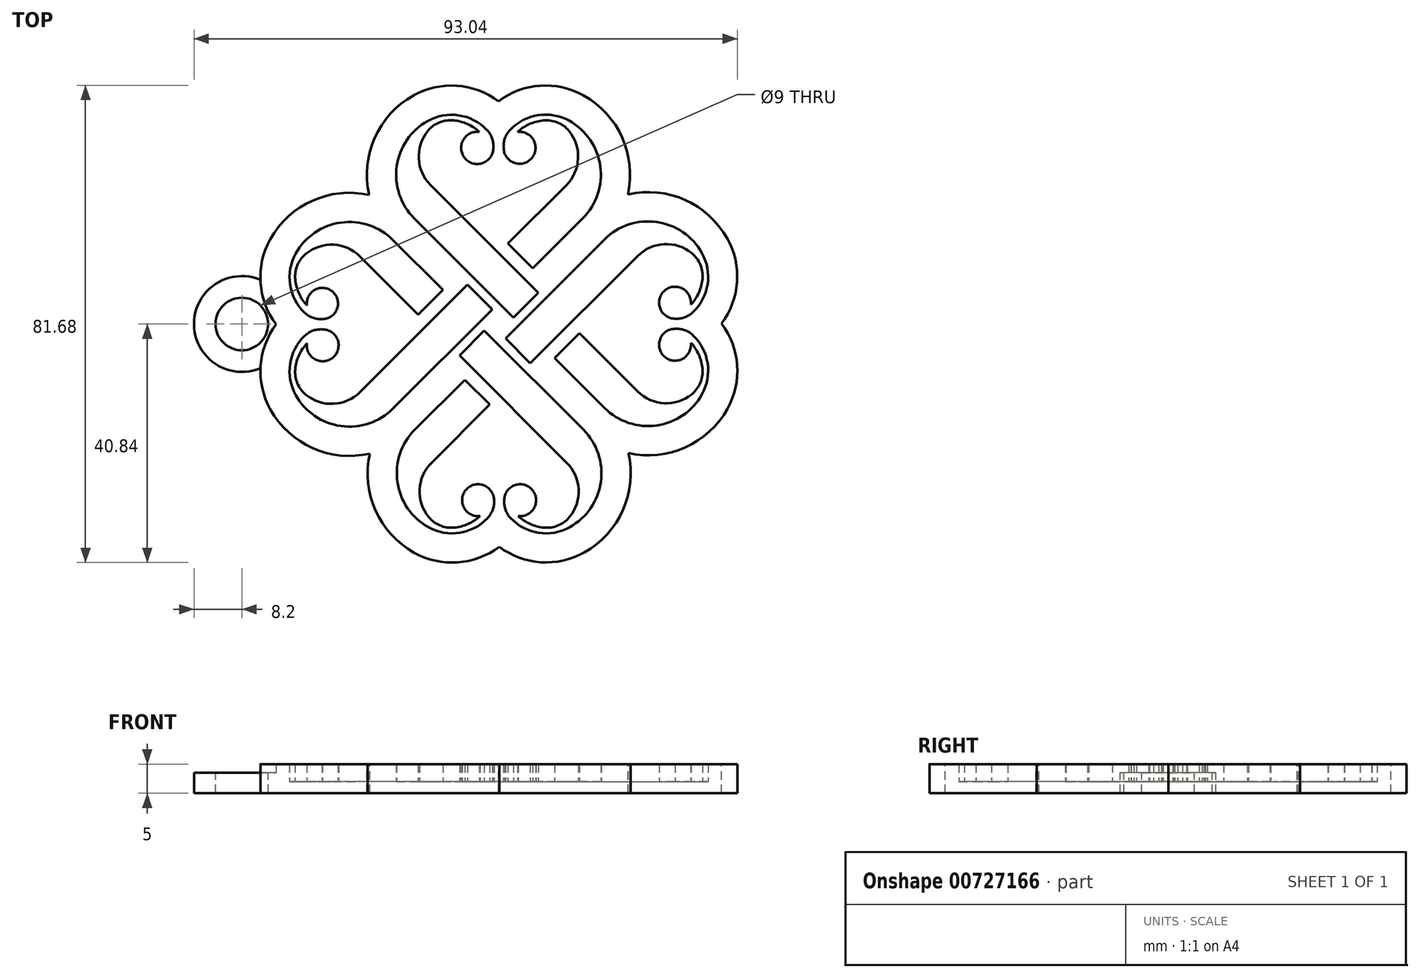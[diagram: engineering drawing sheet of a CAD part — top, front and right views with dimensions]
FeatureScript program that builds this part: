
annotation { "Feature Type Name" : "Feature", "Feature Type Description" : "" }
export const myFeature = defineFeature(function(context is Context, id is Id, definition is map)
    precondition{}
    {
        {
            var Q0;
            Q0=qCreatedBy(makeId("Top.planeOp"),FACE);
            var sketch = newSketch(context, id + "F0", { "sketchPlane" : qUnion([Q0])});
            skLineSegment(sketch, "E0", {"start": v(2.5, 1.1) * mm, "end": v(6.73, 5.35) * mm});
            skLineSegment(sketch, "E1", {"start": v(2.5, 1.1) * mm, "end": v(-14.5, 18.1) * mm});
            skLineSegment(sketch, "E2", {"start": v(6.73, 5.35) * mm, "end": v(-11.69, 23.78) * mm});
            skArc(sketch, "E3", {"start": v(-11.69, 23.78) * mm, "mid": v(-13.7, 28.32) * mm, "end": v(-12.15, 33.05) * mm});
            skArc(sketch, "E4", {"start": v(-12.15, 33.05) * mm, "mid": v(-10.18, 34.5) * mm, "end": v(-7.75, 34.87) * mm});
            skArc(sketch, "E5", {"start": v(-7.75, 34.87) * mm, "mid": v(-5.39, 34.24) * mm, "end": v(-3.34, 32.88) * mm});
            skArc(sketch, "E6", {"start": v(-14.5, 18.1) * mm, "mid": v(-17.48, 27) * mm, "end": v(-12.18, 34.76) * mm});
            skArc(sketch, "E7", {"start": v(-12.18, 34.76) * mm, "mid": v(-6.85, 35.73) * mm, "end": v(-2.04, 33.22) * mm});
            skArc(sketch, "E8", {"start": v(-3.34, 32.88) * mm, "mid": v(-5.75, 28.32) * mm, "end": v(-0.94, 30.19) * mm});
            skArc(sketch, "E9", {"start": v(-2.04, 33.22) * mm, "mid": v(-1.17, 31.82) * mm, "end": v(-0.94, 30.19) * mm});
            skLineSegment(sketch, "E10", {"start": v(1.14, -2.5) * mm, "end": v(5.39, -6.73) * mm});
            skLineSegment(sketch, "E11", {"start": v(1.14, -2.5) * mm, "end": v(18.11, 14.48) * mm});
            skLineSegment(sketch, "E12", {"start": v(5.39, -6.73) * mm, "end": v(23.77, 11.65) * mm});
            skArc(sketch, "E13", {"start": v(23.77, 11.65) * mm, "mid": v(28.31, 13.67) * mm, "end": v(33.03, 12.12) * mm});
            skArc(sketch, "E14", {"start": v(33.03, 12.12) * mm, "mid": v(34.5, 10.15) * mm, "end": v(34.86, 7.72) * mm});
            skArc(sketch, "E15", {"start": v(34.86, 7.72) * mm, "mid": v(34.23, 5.35) * mm, "end": v(32.88, 3.3) * mm});
            skArc(sketch, "E16", {"start": v(18.11, 14.48) * mm, "mid": v(27.02, 17.47) * mm, "end": v(34.78, 12.16) * mm});
            skArc(sketch, "E17", {"start": v(34.78, 12.16) * mm, "mid": v(35.74, 6.83) * mm, "end": v(33.24, 2.02) * mm});
            skArc(sketch, "E18", {"start": v(32.88, 3.3) * mm, "mid": v(28.35, 5.69) * mm, "end": v(30.2, 0.92) * mm});
            skArc(sketch, "E19", {"start": v(33.24, 2.02) * mm, "mid": v(31.84, 1.15) * mm, "end": v(30.2, 0.92) * mm});
            skLineSegment(sketch, "E20", {"start": v(-2.5, -1.14) * mm, "end": v(-6.73, -5.39) * mm});
            skLineSegment(sketch, "E21", {"start": v(-2.5, -1.14) * mm, "end": v(14.48, -18.11) * mm});
            skLineSegment(sketch, "E22", {"start": v(-6.73, -5.39) * mm, "end": v(11.65, -23.77) * mm});
            skArc(sketch, "E23", {"start": v(11.65, -23.77) * mm, "mid": v(13.67, -28.31) * mm, "end": v(12.12, -33.03) * mm});
            skArc(sketch, "E24", {"start": v(12.12, -33.03) * mm, "mid": v(10.15, -34.5) * mm, "end": v(7.72, -34.86) * mm});
            skArc(sketch, "E25", {"start": v(7.72, -34.86) * mm, "mid": v(5.35, -34.23) * mm, "end": v(3.3, -32.88) * mm});
            skArc(sketch, "E26", {"start": v(14.48, -18.11) * mm, "mid": v(17.47, -27.02) * mm, "end": v(12.16, -34.78) * mm});
            skArc(sketch, "E27", {"start": v(12.16, -34.78) * mm, "mid": v(6.83, -35.74) * mm, "end": v(2.02, -33.24) * mm});
            skArc(sketch, "E28", {"start": v(3.3, -32.88) * mm, "mid": v(5.69, -28.35) * mm, "end": v(0.92, -30.2) * mm});
            skArc(sketch, "E29", {"start": v(2.02, -33.24) * mm, "mid": v(1.15, -31.84) * mm, "end": v(0.92, -30.2) * mm});
            skLineSegment(sketch, "E30", {"start": v(-1.14, 2.5) * mm, "end": v(-5.39, 6.73) * mm});
            skLineSegment(sketch, "E31", {"start": v(-1.14, 2.5) * mm, "end": v(-18.11, -14.48) * mm});
            skLineSegment(sketch, "E32", {"start": v(-5.39, 6.73) * mm, "end": v(-23.77, -11.65) * mm});
            skArc(sketch, "E33", {"start": v(-23.77, -11.65) * mm, "mid": v(-28.31, -13.67) * mm, "end": v(-33.03, -12.12) * mm});
            skArc(sketch, "E34", {"start": v(-33.03, -12.12) * mm, "mid": v(-34.5, -10.15) * mm, "end": v(-34.86, -7.72) * mm});
            skArc(sketch, "E35", {"start": v(-34.86, -7.72) * mm, "mid": v(-34.23, -5.35) * mm, "end": v(-32.88, -3.3) * mm});
            skArc(sketch, "E36", {"start": v(-18.11, -14.48) * mm, "mid": v(-27.02, -17.47) * mm, "end": v(-34.78, -12.16) * mm});
            skArc(sketch, "E37", {"start": v(-34.78, -12.16) * mm, "mid": v(-35.74, -6.83) * mm, "end": v(-33.24, -2.02) * mm});
            skArc(sketch, "E38", {"start": v(-32.88, -3.3) * mm, "mid": v(-28.35, -5.69) * mm, "end": v(-30.2, -0.92) * mm});
            skArc(sketch, "E39", {"start": v(-33.24, -2.02) * mm, "mid": v(-31.84, -1.15) * mm, "end": v(-30.2, -0.92) * mm});
            skArc(sketch, "E40.MirrorCS", {"start": v(11.55, 23.77) * mm, "mid": v(13.57, 28.31) * mm, "end": v(12.02, 33.03) * mm});
            skArc(sketch, "E41.MirrorCS", {"start": v(1.93, 33.24) * mm, "mid": v(1.06, 31.84) * mm, "end": v(0.82, 30.2) * mm});
            skArc(sketch, "E42.MirrorCS", {"start": v(3.2, 32.88) * mm, "mid": v(5.6, 28.35) * mm, "end": v(0.82, 30.2) * mm});
            skArc(sketch, "E43.MirrorCS", {"start": v(7.62, 34.86) * mm, "mid": v(5.25, 34.23) * mm, "end": v(3.2, 32.88) * mm});
            skArc(sketch, "E44.MirrorCS", {"start": v(12.02, 33.03) * mm, "mid": v(10.05, 34.5) * mm, "end": v(7.62, 34.86) * mm});
            skArc(sketch, "E45.MirrorCS", {"start": v(12.06, 34.78) * mm, "mid": v(6.73, 35.74) * mm, "end": v(1.93, 33.24) * mm});
            skArc(sketch, "E46.MirrorCS", {"start": v(14.38, 18.11) * mm, "mid": v(17.37, 27.02) * mm, "end": v(12.06, 34.78) * mm});
            skLineSegment(sketch, "E47.trimOffspring", {"start": v(1.58, 13.8) * mm, "end": v(11.55, 23.77) * mm});
            skLineSegment(sketch, "E48.trimOffspring", {"start": v(5.82, 9.55) * mm, "end": v(14.38, 18.11) * mm});
            skArc(sketch, "E49.MirrorCS", {"start": v(23.77, -11.55) * mm, "mid": v(28.31, -13.57) * mm, "end": v(33.03, -12.02) * mm});
            skArc(sketch, "E50.MirrorCS", {"start": v(33.24, -1.93) * mm, "mid": v(31.84, -1.06) * mm, "end": v(30.2, -0.82) * mm});
            skArc(sketch, "E51.MirrorCS", {"start": v(32.88, -3.2) * mm, "mid": v(28.35, -5.6) * mm, "end": v(30.2, -0.82) * mm});
            skArc(sketch, "E52.MirrorCS", {"start": v(34.86, -7.62) * mm, "mid": v(34.23, -5.25) * mm, "end": v(32.88, -3.2) * mm});
            skArc(sketch, "E53.MirrorCS", {"start": v(33.03, -12.02) * mm, "mid": v(34.5, -10.05) * mm, "end": v(34.86, -7.62) * mm});
            skArc(sketch, "E54.MirrorCS", {"start": v(34.78, -12.06) * mm, "mid": v(35.74, -6.73) * mm, "end": v(33.24, -1.93) * mm});
            skArc(sketch, "E55.MirrorCS", {"start": v(18.11, -14.38) * mm, "mid": v(27.02, -17.37) * mm, "end": v(34.78, -12.06) * mm});
            skLineSegment(sketch, "E56.trimOffspring", {"start": v(13.8, -1.58) * mm, "end": v(23.77, -11.55) * mm});
            skLineSegment(sketch, "E57.trimOffspring", {"start": v(9.55, -5.82) * mm, "end": v(18.11, -14.38) * mm});
            skArc(sketch, "E58.MirrorCS", {"start": v(-11.55, -23.77) * mm, "mid": v(-13.57, -28.31) * mm, "end": v(-12.02, -33.03) * mm});
            skArc(sketch, "E59.MirrorCS", {"start": v(-1.93, -33.24) * mm, "mid": v(-1.06, -31.84) * mm, "end": v(-0.82, -30.2) * mm});
            skArc(sketch, "E60.MirrorCS", {"start": v(-3.2, -32.88) * mm, "mid": v(-5.6, -28.35) * mm, "end": v(-0.82, -30.2) * mm});
            skArc(sketch, "E61.MirrorCS", {"start": v(-7.62, -34.86) * mm, "mid": v(-5.25, -34.23) * mm, "end": v(-3.2, -32.88) * mm});
            skArc(sketch, "E62.MirrorCS", {"start": v(-12.02, -33.03) * mm, "mid": v(-10.05, -34.5) * mm, "end": v(-7.62, -34.86) * mm});
            skArc(sketch, "E63.MirrorCS", {"start": v(-12.06, -34.78) * mm, "mid": v(-6.73, -35.74) * mm, "end": v(-1.93, -33.24) * mm});
            skArc(sketch, "E64.MirrorCS", {"start": v(-14.38, -18.11) * mm, "mid": v(-17.37, -27.02) * mm, "end": v(-12.06, -34.78) * mm});
            skLineSegment(sketch, "E65.trimOffspring", {"start": v(-1.58, -13.8) * mm, "end": v(-11.55, -23.77) * mm});
            skLineSegment(sketch, "E66.trimOffspring", {"start": v(-5.82, -9.55) * mm, "end": v(-14.38, -18.11) * mm});
            skArc(sketch, "E67.MirrorCS", {"start": v(-23.77, 11.55) * mm, "mid": v(-28.31, 13.57) * mm, "end": v(-33.03, 12.02) * mm});
            skArc(sketch, "E68.MirrorCS", {"start": v(-33.24, 1.93) * mm, "mid": v(-31.86, 1.07) * mm, "end": v(-30.25, 0.84) * mm});
            skArc(sketch, "E69.MirrorCS", {"start": v(-32.86, 3.17) * mm, "mid": v(-28.43, 5.5) * mm, "end": v(-30.25, 0.84) * mm});
            skArc(sketch, "E70.MirrorCS", {"start": v(-34.86, 7.62) * mm, "mid": v(-34.22, 5.23) * mm, "end": v(-32.86, 3.17) * mm});
            skArc(sketch, "E71.MirrorCS", {"start": v(-33.03, 12.02) * mm, "mid": v(-34.5, 10.05) * mm, "end": v(-34.86, 7.62) * mm});
            skArc(sketch, "E72.MirrorCS", {"start": v(-34.78, 12.06) * mm, "mid": v(-35.74, 6.73) * mm, "end": v(-33.24, 1.93) * mm});
            skArc(sketch, "E73.MirrorCS", {"start": v(-18.11, 14.38) * mm, "mid": v(-27.02, 17.37) * mm, "end": v(-34.78, 12.06) * mm});
            skLineSegment(sketch, "E74.trimOffspring", {"start": v(-13.84, 1.62) * mm, "end": v(-23.77, 11.55) * mm});
            skLineSegment(sketch, "E75.trimOffspring", {"start": v(-9.6, 5.86) * mm, "end": v(-18.11, 14.38) * mm});
            skArc(sketch, "E76.2", {"start": v(-39.14, 14.5) * mm, "mid": v(-40.8, 7.07) * mm, "end": v(-38.14, -0.07) * mm});
            skArc(sketch, "E76.5", {"start": v(-22.2, 22.1) * mm, "mid": v(-31.93, 21.11) * mm, "end": v(-39.14, 14.5) * mm});
            skArc(sketch, "E77.2", {"start": v(-14.61, 39.13) * mm, "mid": v(-7.2, 40.8) * mm, "end": v(-0.07, 38.14) * mm});
            skArc(sketch, "E77.5", {"start": v(-22.2, 22.1) * mm, "mid": v(-21.24, 31.88) * mm, "end": v(-14.61, 39.13) * mm});
            skLineSegment(sketch, "E78", {"start": v(0, 40.38) * mm, "end": v(0, -16.8) * mm, "construction": true});
            skArc(sketch, "E79.1.0", {"start": v(-39.13, -14.61) * mm, "mid": v(-40.8, -7.2) * mm, "end": v(-38.14, -0.07) * mm});
            skArc(sketch, "E79.1.1", {"start": v(-22.1, -22.2) * mm, "mid": v(-31.88, -21.24) * mm, "end": v(-39.13, -14.61) * mm});
            skArc(sketch, "E79.1.2", {"start": v(-22.1, -22.2) * mm, "mid": v(-21.11, -31.93) * mm, "end": v(-14.5, -39.14) * mm});
            skArc(sketch, "E79.1.3", {"start": v(-14.5, -39.14) * mm, "mid": v(-7.07, -40.8) * mm, "end": v(0.07, -38.14) * mm});
            skArc(sketch, "E79.2.0", {"start": v(14.61, -39.13) * mm, "mid": v(7.2, -40.8) * mm, "end": v(0.07, -38.14) * mm});
            skArc(sketch, "E79.2.1", {"start": v(22.2, -22.1) * mm, "mid": v(21.24, -31.88) * mm, "end": v(14.61, -39.13) * mm});
            skArc(sketch, "E79.2.2", {"start": v(22.2, -22.1) * mm, "mid": v(31.93, -21.11) * mm, "end": v(39.14, -14.5) * mm});
            skArc(sketch, "E79.2.3", {"start": v(39.14, -14.5) * mm, "mid": v(40.8, -7.07) * mm, "end": v(38.14, 0.07) * mm});
            skArc(sketch, "E79.3.0", {"start": v(39.13, 14.61) * mm, "mid": v(40.8, 7.2) * mm, "end": v(38.14, 0.07) * mm});
            skArc(sketch, "E79.3.1", {"start": v(22.1, 22.2) * mm, "mid": v(31.88, 21.24) * mm, "end": v(39.13, 14.61) * mm});
            skArc(sketch, "E79.3.2", {"start": v(22.1, 22.2) * mm, "mid": v(21.11, 31.93) * mm, "end": v(14.5, 39.14) * mm});
            skArc(sketch, "E79.3.3", {"start": v(14.5, 39.14) * mm, "mid": v(7.07, 40.8) * mm, "end": v(-0.07, 38.14) * mm});
            skPoint(sketch, "E79.center", {"position": v(0, 0) * mm});
            skPoint(sketch, "E80.orphan", {"position": v(0, 38.19) * mm});
            skPoint(sketch, "E81.orphan", {"position": v(0, 38.09) * mm});
            skPoint(sketch, "E82.orphan", {"position": v(38.19, 0) * mm});
            skPoint(sketch, "E83.orphan", {"position": v(38.09, 0) * mm});
            skPoint(sketch, "E84.orphan", {"position": v(0, -38.19) * mm});
            skPoint(sketch, "E85.orphan", {"position": v(0, -38.09) * mm});
            skPoint(sketch, "E86.orphan", {"position": v(-38.19, 0) * mm});
            skPoint(sketch, "E87.orphan", {"position": v(-38.09, 0) * mm});
            skArc(sketch, "E88", {"start": v(-40.83, 7.56) * mm, "mid": v(-52.2, -0.01) * mm, "end": v(-40.8, -7.55) * mm});
            skCircle(sketch, "E89", {"center": v(-44, 0) * mm, "radius": 4.5 * mm});
            skLineSegment(sketch, "E90.0", {"start": v(-13.84, 1.62) * mm, "end": v(-9.6, 5.86) * mm});
            skLineSegment(sketch, "E91.0", {"start": v(-1.58, -13.8) * mm, "end": v(-5.82, -9.55) * mm});
            skLineSegment(sketch, "E92.0", {"start": v(13.8, -1.58) * mm, "end": v(9.55, -5.82) * mm});
            skLineSegment(sketch, "E93.0", {"start": v(1.58, 13.8) * mm, "end": v(5.82, 9.55) * mm});
            skSolve(sketch);
        }
        {
            var Q0;
            Q0=makeQuery(id+"F0.imprint","IMPRINT",FACE,{"disambiguationData":[TD([[makeQuery(id+"F0.imprint","IMPRINT",EDGE,{"derivedFrom":sQuery(id+"F0.wireOp",EDGE,"E0")}),-1.0]])]});
            var Q1;
            Q1=makeQuery(id+"F0.imprint","IMPRINT",FACE,{"disambiguationData":[TD([[makeQuery(id+"F0.imprint","IMPRINT",EDGE,{"derivedFrom":sQuery(id+"F0.wireOp",EDGE,"E0")}),1.0]])]});
            var Q2;
            Q2=makeQuery(id+"F0.imprint","IMPRINT",FACE,{"disambiguationData":[TD([[makeQuery(id+"F0.imprint","IMPRINT",EDGE,{"derivedFrom":sQuery(id+"F0.wireOp",EDGE,"E40.MirrorCS")}),-1.0]])]});
            var Q3;
            Q3=makeQuery(id+"F0.imprint","IMPRINT",FACE,{"disambiguationData":[TD([[makeQuery(id+"F0.imprint","IMPRINT",EDGE,{"derivedFrom":sQuery(id+"F0.wireOp",EDGE,"E10")}),1.0]])]});
            var Q4;
            Q4=makeQuery(id+"F0.imprint","IMPRINT",FACE,{"disambiguationData":[TD([[makeQuery(id+"F0.imprint","IMPRINT",EDGE,{"derivedFrom":sQuery(id+"F0.wireOp",EDGE,"E49.MirrorCS")}),-1.0]])]});
            var Q5;
            Q5=makeQuery(id+"F0.imprint","IMPRINT",FACE,{"disambiguationData":[TD([[makeQuery(id+"F0.imprint","IMPRINT",EDGE,{"derivedFrom":sQuery(id+"F0.wireOp",EDGE,"E20")}),1.0]])]});
            var Q6;
            Q6=makeQuery(id+"F0.imprint","IMPRINT",FACE,{"disambiguationData":[TD([[makeQuery(id+"F0.imprint","IMPRINT",EDGE,{"derivedFrom":sQuery(id+"F0.wireOp",EDGE,"E58.MirrorCS")}),-1.0]])]});
            var Q7;
            Q7=makeQuery(id+"F0.imprint","IMPRINT",FACE,{"disambiguationData":[TD([[makeQuery(id+"F0.imprint","IMPRINT",EDGE,{"derivedFrom":sQuery(id+"F0.wireOp",EDGE,"E30")}),1.0]])]});
            var Q8;
            Q8=makeQuery(id+"F0.imprint","IMPRINT",FACE,{"disambiguationData":[TD([[makeQuery(id+"F0.imprint","IMPRINT",EDGE,{"derivedFrom":sQuery(id+"F0.wireOp",EDGE,"E67.MirrorCS")}),-1.0]])]});
            var Q9;
            {var subQ3=sQuery(id+"F0.wireOp",EDGE,"E88");Q9=makeQuery(id+"F0.imprint","IMPRINT",FACE,{"disambiguationData":[TD([[makeQuery(id+"F0.imprint","IMPRINT",EDGE,{"derivedFrom":subQ3}),1.0]])]});}
            extrude(context, id + "F1", {"entities" : qUnion([Q0, Q1, Q2, Q3, Q4, Q5, Q6, Q7, Q8, Q9]), "oppositeDirection" : true, "depth" : 2 * mm, "offsetDistance" : 25 * mm});
        }
        {
            var Q0;
            Q0=makeQuery(id+"F0.imprint","IMPRINT",FACE,{"disambiguationData":[TD([[makeQuery(id+"F0.imprint","IMPRINT",EDGE,{"derivedFrom":sQuery(id+"F0.wireOp",EDGE,"E0")}),-1.0]])]});
            extrude(context, id + "F2", {"entities" : qUnion([Q0]), "operationType" : NewBodyOperationType.ADD, "depth" : 3 * mm, "offsetDistance" : 25 * mm});
        }
        {
            var Q0;
            {var subQ3=sQuery(id+"F0.wireOp",EDGE,"E88");Q0=makeQuery(id+"F0.imprint","IMPRINT",FACE,{"disambiguationData":[TD([[makeQuery(id+"F0.imprint","IMPRINT",EDGE,{"derivedFrom":subQ3}),1.0]])]});}
            extrude(context, id + "F3", {"entities" : qUnion([Q0]), "operationType" : NewBodyOperationType.ADD, "depth" : 1.5 * mm, "offsetDistance" : 25 * mm});
        }
    });
